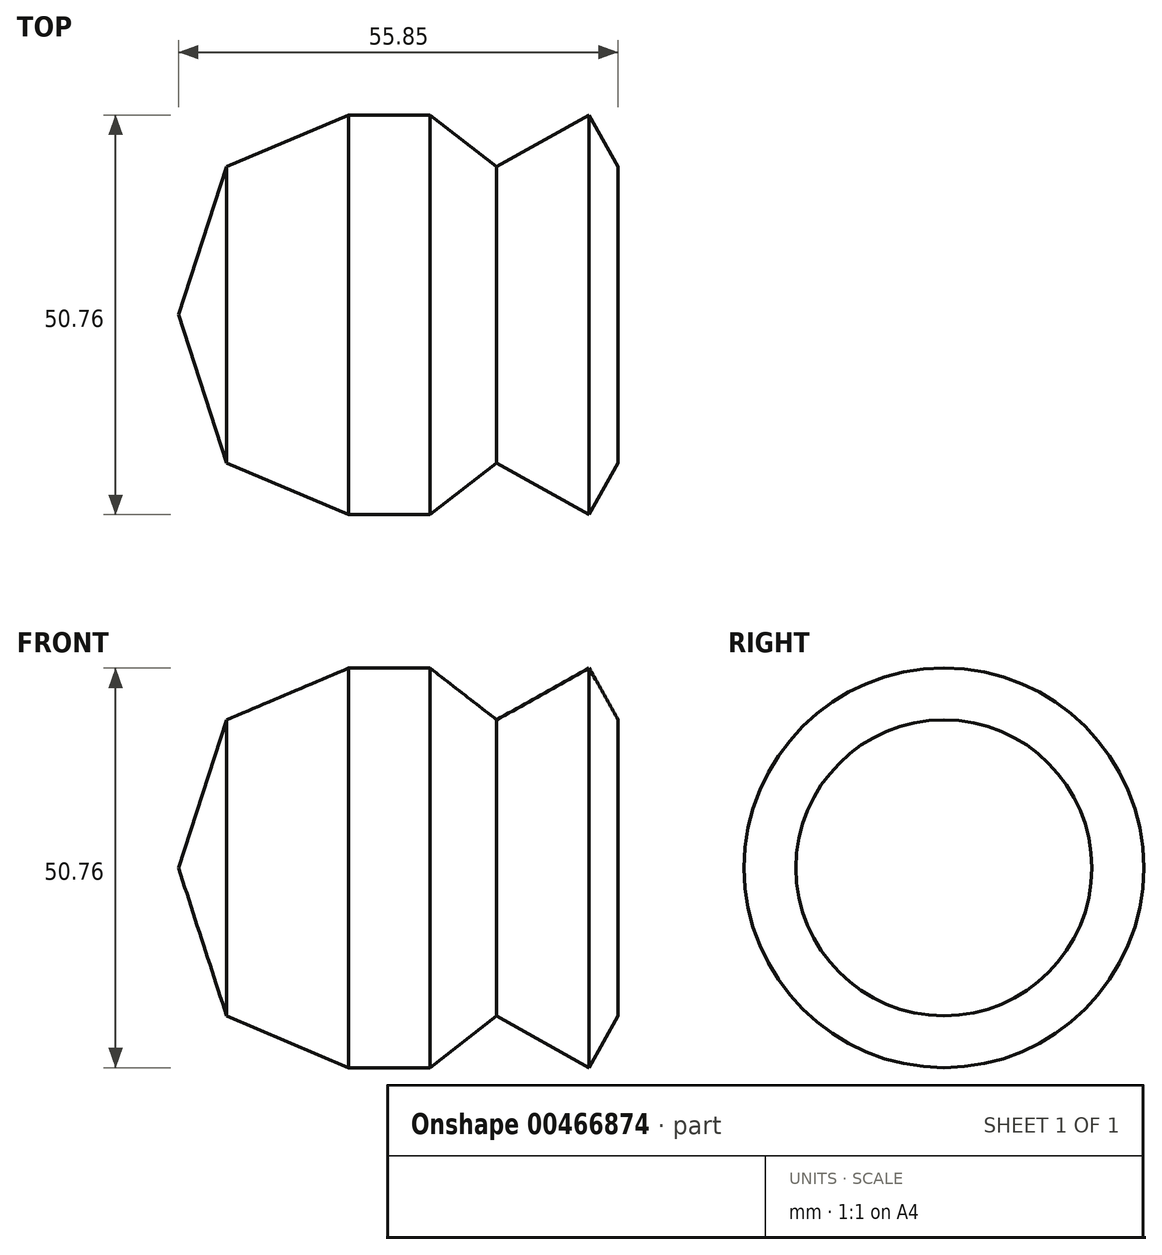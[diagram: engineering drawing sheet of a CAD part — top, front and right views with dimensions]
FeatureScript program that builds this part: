
annotation { "Feature Type Name" : "Feature", "Feature Type Description" : "" }
export const myFeature = defineFeature(function(context is Context, id is Id, definition is map)
    precondition{}
    {
        {
            var Q0;
            Q0=qCreatedBy(makeId("Top.planeOp"),FACE);
            var sketch = newSketch(context, id + "F0", { "sketchPlane" : qUnion([Q0])});
            skLineSegment(sketch, "E0", {"start": v(0, 0) * mm, "end": v(6.1, 18.8) * mm});
            skLineSegment(sketch, "E1", {"start": v(6.1, 18.8) * mm, "end": v(21.62, 25.38) * mm});
            skLineSegment(sketch, "E2", {"start": v(21.62, 25.38) * mm, "end": v(31.96, 25.38) * mm});
            skLineSegment(sketch, "E3", {"start": v(31.96, 25.38) * mm, "end": v(40.42, 18.8) * mm});
            skLineSegment(sketch, "E4", {"start": v(40.42, 18.8) * mm, "end": v(52.17, 25.38) * mm});
            skLineSegment(sketch, "E5", {"start": v(52.17, 25.38) * mm, "end": v(55.85, 18.8) * mm});
            skLineSegment(sketch, "E6", {"start": v(0, 0) * mm, "end": v(55.85, 0) * mm});
            skLineSegment(sketch, "E7", {"start": v(55.85, 0) * mm, "end": v(55.85, 18.8) * mm});
            skSolve(sketch);
        }
        {
            var Q0;
            Q0=makeQuery(id+"F0.imprint","IMPRINT",FACE,{"disambiguationData":[TD([[makeQuery(id+"F0.imprint","IMPRINT",EDGE,{"derivedFrom":sQuery(id+"F0.wireOp",EDGE,"E0")}),-1.0]])]});
            var Q1;
            Q1=sQuery(id+"F0.wireOp",EDGE,"E6");
            revolve(context, id + "F1", {"entities" : qUnion([Q0]), "axis" : qUnion([Q1]), "revolveType" : RevolveType.FULL});
        }
    });
